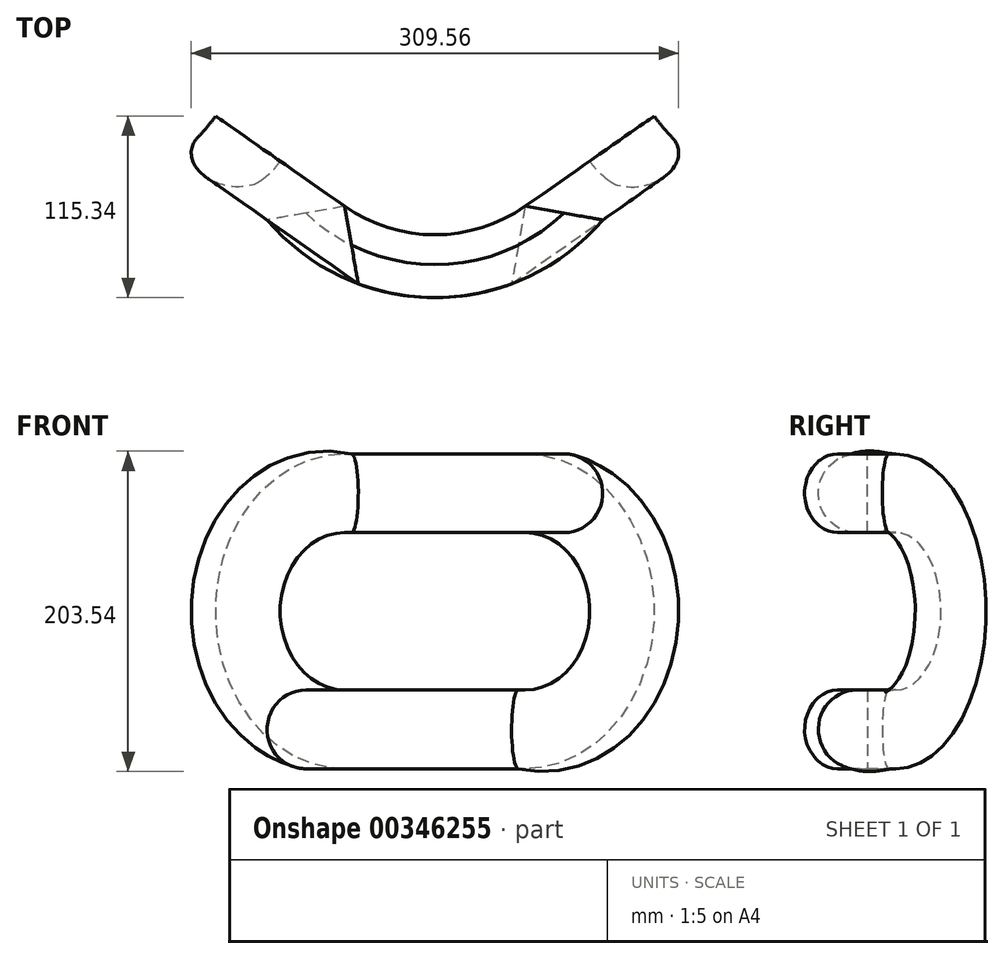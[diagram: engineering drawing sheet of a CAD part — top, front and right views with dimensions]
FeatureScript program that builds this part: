
annotation { "Feature Type Name" : "Feature", "Feature Type Description" : "" }
export const myFeature = defineFeature(function(context is Context, id is Id, definition is map)
    precondition{}
    {
        {
            var Q0;
            Q0=qCreatedBy(makeId("Top.planeOp"),FACE);
            var sketch = newSketch(context, id + "F0", { "sketchPlane" : qUnion([Q0])});
            skArc(sketch, "E0", {"start": v(-57.36, -81.92) * mm, "mid": v(0, -100) * mm, "end": v(57.36, -81.92) * mm});
            skLineSegment(sketch, "E1", {"start": v(0, 0) * mm, "end": v(-57.36, -81.92) * mm, "construction": true});
            skArc(sketch, "E2.MirrorC", {"start": v(57.36, -81.92) * mm, "mid": v(0, -100) * mm, "end": v(-57.36, -81.92) * mm});
            skLineSegment(sketch, "E3", {"start": v(0, 0) * mm, "end": v(0, -100) * mm});
            skLineSegment(sketch, "E4.MirrorCS", {"start": v(0, 0) * mm, "end": v(57.36, -81.92) * mm, "construction": true});
            skLineSegment(sketch, "E5", {"start": v(-57.36, -81.92) * mm, "end": v(-204.91, 21.4) * mm});
            skLineSegment(sketch, "E6", {"start": v(57.36, -81.92) * mm, "end": v(231.4, 39.95) * mm});
            skSolve(sketch);
        }
        {
            var Q0;
            Q0 = qSketchRegion(id + "F0", true);
            var Q1;
            Q1=sQuery(id+"F0.wireOp",EDGE,"E5");
            var Q2;
            Q2=sQuery(id+"F0.wireOp",EDGE,"E0");
            var Q3;
            Q3=sQuery(id+"F0.wireOp",EDGE,"E6");
            extrude(context, id + "F1", {"entities" : qUnion([Q0]), "bodyType" : ToolBodyType.SURFACE, "surfaceEntities" : qUnion([Q1, Q2, Q3]), "depth" : 50 * mm, "hasSecondDirection" : true, "secondDirectionOppositeDirection" : true, "secondDirectionDepth" : 50 * mm});
        }
        {
            var Q0;
            Q0=makeQuery(id+"F1.opExtrude","SWEPT_FACE",FACE,{"disambiguationData":[OSD([sQuery(id+"F0.wireOp",EDGE,"E5")])]});
            var sketch = newSketch(context, id + "F2", { "sketchPlane" : qUnion([Q0])});
            skArc(sketch, "E7", {"start": v(0, -50) * mm, "mid": v(50, 0) * mm, "end": v(0, 50) * mm});
            skSolve(sketch);
        }
        {
            var Q0;
            Q0=makeQuery(id+"F1.opExtrude","SWEPT_FACE",FACE,{"disambiguationData":[OSD([sQuery(id+"F0.wireOp",EDGE,"E6")])]});
            var sketch = newSketch(context, id + "F3", { "sketchPlane" : qUnion([Q0])});
            skArc(sketch, "E8", {"start": v(0, 50) * mm, "mid": v(-50, 0) * mm, "end": v(0, -50) * mm});
            skSolve(sketch);
        }
        {
            var Q0;
            Q0=makeQuery(id+"F1.opExtrude","SWEPT_EDGE",EDGE,{"disambiguationData":[OSD([sQuery(id+"F0.wireOp",VERTEX,"E0.start")])]});
            var Q1;
            Q1=sQuery(id+"F2.wireOp",EDGE,"E7");
            cPlane(context, id + "F4", {"entities" : qUnion([Q0, Q1]), "cplaneType" : CPlaneType.LINE_ANGLE, "offset" : 100 * mm, "angle" : 45 * degree, "width" : 150 * mm, "height" : 150 * mm});
        }
        {
            var Q0;
            Q0=qCreatedBy(id+"F4.planeOp",FACE);
            var sketch = newSketch(context, id + "F5", { "sketchPlane" : qUnion([Q0])});
            skLineSegment(sketch, "E9.bottom", {"start": v(70.71, 100) * mm, "end": v(95.71, 100) * mm});
            skLineSegment(sketch, "E9.top", {"start": v(70.71, 50) * mm, "end": v(95.71, 50) * mm});
            skLineSegment(sketch, "E9.left", {"start": v(70.71, 100) * mm, "end": v(70.71, 50) * mm});
            skArc(sketch, "E10", {"start": v(95.71, 50) * mm, "mid": v(120.71, 75) * mm, "end": v(95.71, 100) * mm});
            skPoint(sketch, "E10.centerSnap0", {"position": v(95.71, 50) * mm});
            skPoint(sketch, "E10.centerSnap1", {"position": v(70.71, 75) * mm});
            skPoint(sketch, "E11.orphan", {"position": v(120.71, 50) * mm});
            skSolve(sketch);
        }
        {
            var Q0;
            Q0=makeQuery(id+"F5.imprint","IMPRINT",FACE,{"disambiguationData":[TD([[makeQuery(id+"F5.imprint","IMPRINT",EDGE,{"derivedFrom":sQuery(id+"F5.wireOp",EDGE,"E9.bottom")}),-1.0]])]});
            var Q1;
            Q1=sQuery(id+"F2.wireOp",EDGE,"E7");
            var Q2;
            Q2=makeQuery(id+"F1.opExtrude","CAP_EDGE",EDGE,{"disambiguationData":[OSD([sQuery(id+"F0.wireOp",EDGE,"E0")])],"isStart":true});
            var Q3;
            Q3=sQuery(id+"F3.wireOp",EDGE,"E8");
            var Q4;
            Q4=makeQuery(id+"F1.opExtrude","CAP_EDGE",EDGE,{"disambiguationData":[OSD([sQuery(id+"F0.wireOp",EDGE,"E0")])],"isStart":false});
            sweep(context, id + "F6", {"profiles" : qUnion([Q0]), "path" : qUnion([Q1, Q2, Q3, Q4])});
        }
    });
